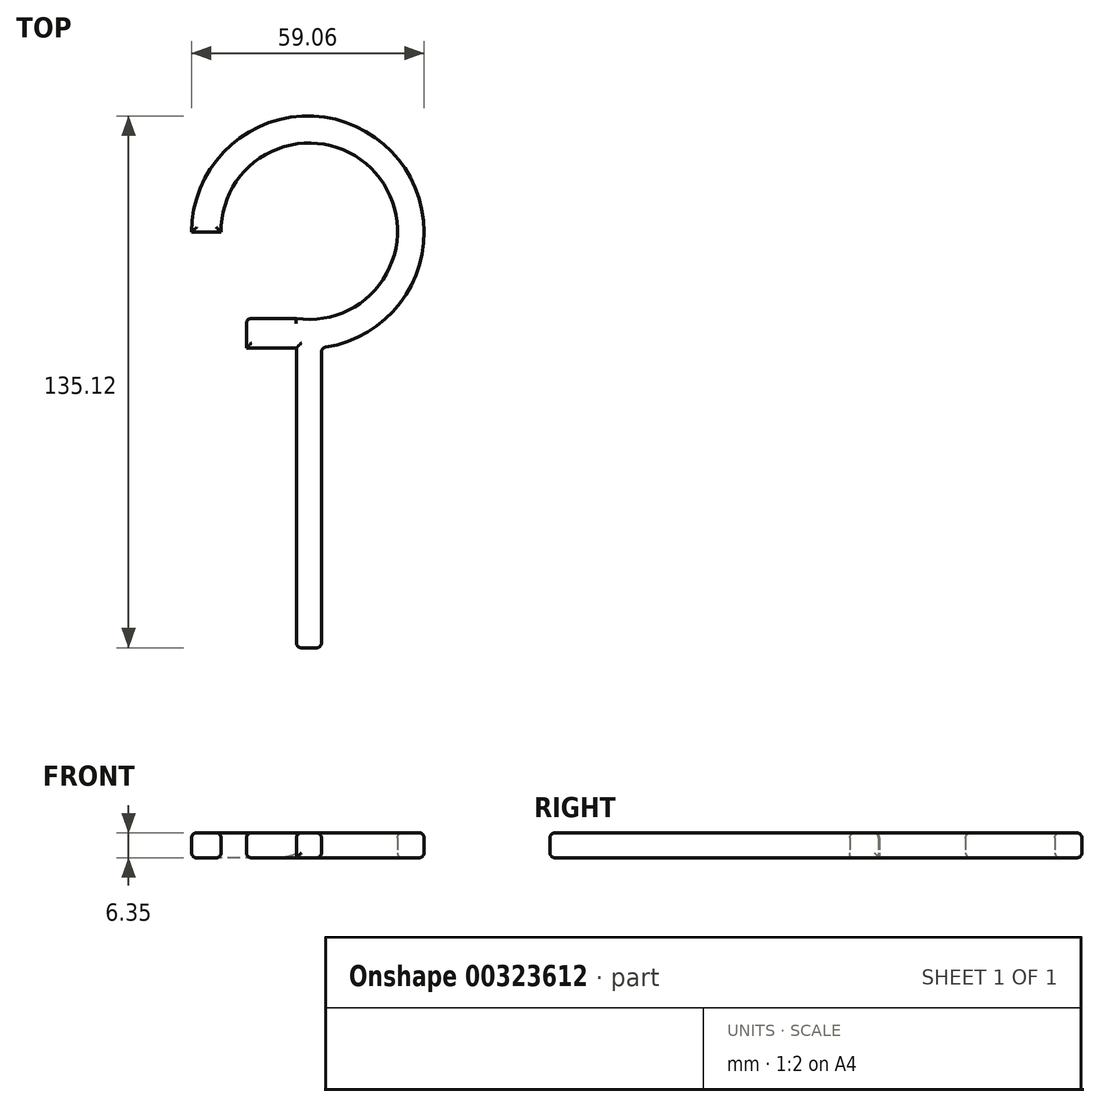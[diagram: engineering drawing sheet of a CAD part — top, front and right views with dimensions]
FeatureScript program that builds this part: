
annotation { "Feature Type Name" : "Feature", "Feature Type Description" : "" }
export const myFeature = defineFeature(function(context is Context, id is Id, definition is map)
    precondition{}
    {
        {
            var Q0;
            Q0=qCreatedBy(makeId("Top.planeOp"),FACE);
            var sketch = newSketch(context, id + "F0", { "sketchPlane" : qUnion([Q0])});
            skArc(sketch, "E0", {"start": v(-2.9, -29.39) * mm, "mid": v(21.88, 19.83) * mm, "end": v(-29.53, 0) * mm});
            skLineSegment(sketch, "E1.left", {"start": v(-2.9, -29.39) * mm, "end": v(-2.9, -105.59) * mm});
            skLineSegment(sketch, "E1.right", {"start": v(3.46, -29.33) * mm, "end": v(3.46, -105.59) * mm});
            skLineSegment(sketch, "E2", {"start": v(-29.53, 0) * mm, "end": v(-22.04, 0) * mm});
            skLineSegment(sketch, "E3", {"start": v(-2.9, -29.39) * mm, "end": v(-2.9, -21.9) * mm});
            skArc(sketch, "E4", {"start": v(-2.9, -21.9) * mm, "mid": v(17.23, 15.02) * mm, "end": v(-22.04, 0) * mm});
            skLineSegment(sketch, "E5", {"start": v(0, -21.9) * mm, "end": v(-15.6, -21.9) * mm});
            skLineSegment(sketch, "E6", {"start": v(-15.6, -21.9) * mm, "end": v(-15.6, -29.39) * mm});
            skLineSegment(sketch, "E7", {"start": v(-15.6, -29.39) * mm, "end": v(-2.9, -29.39) * mm});
            skLineSegment(sketch, "E8", {"start": v(-2.9, -105.59) * mm, "end": v(3.46, -105.59) * mm});
            skSolve(sketch);
        }
        {
            var Q0;
            Q0 = qSketchRegion(id + "F0", true);
            extrude(context, id + "F1", {"entities" : qUnion([Q0]), "depth" : 6.35 * mm});
        }
        {
            var Q0;
            Q0=makeQuery(id+"F1.opExtrude","CAP_EDGE",EDGE,{"disambiguationData":[OSD([sQuery(id+"F0.wireOp",EDGE,"E0")])],"isStart":false});
            var Q1;
            Q1=makeQuery(id+"F1.opExtrude","CAP_FACE",FACE,{"disambiguationData":[OSD([sQuery(id+"F0.wireOp",EDGE,"E0"),sQuery(id+"F0.wireOp",EDGE,"E1.bottom"),sQuery(id+"F0.wireOp",EDGE,"E1.top"),sQuery(id+"F0.wireOp",EDGE,"E1.left"),sQuery(id+"F0.wireOp",EDGE,"E1.right"),sQuery(id+"F0.wireOp",EDGE,"E2"),sQuery(id+"F0.wireOp",EDGE,"E3"),sQuery(id+"F0.wireOp",EDGE,"E4")])],"isStart":false});
            var Q2;
            Q2=makeQuery(id+"F1.opExtrude","CAP_EDGE",EDGE,{"disambiguationData":[OSD([sQuery(id+"F0.wireOp",EDGE,"E6")])],"isStart":true});
            var Q3;
            Q3=makeQuery(id+"F1.opExtrude","SWEPT_EDGE",EDGE,{"disambiguationData":[OSD([sQuery(id+"F0.wireOp",EDGE,"E5"),sQuery(id+"F0.wireOp",EDGE,"E6")])]});
            var Q4;
            Q4=makeQuery(id+"F1.opExtrude","CAP_EDGE",EDGE,{"disambiguationData":[OSD([sQuery(id+"F0.wireOp",EDGE,"E1.top")])],"isStart":true});
            var Q5;
            Q5=makeQuery(id+"F1.opExtrude","SWEPT_EDGE",EDGE,{"disambiguationData":[OSD([sQuery(id+"F0.wireOp",EDGE,"E1.top"),sQuery(id+"F0.wireOp",EDGE,"E1.right")])]});
            fillet(context, id + "F2", {"entities" : qUnion([Q0, Q1, Q2, Q3, Q4, Q5]), "radius" : 1.27 * mm, "tangentPropagation" : true, "allowEdgeOverflow" : false});
        }
        {
            var Q0;
            Q0=makeQuery(id+"F1.opExtrude","CAP_EDGE",EDGE,{"disambiguationData":[OSD([sQuery(id+"F0.wireOp",EDGE,"E0")])],"isStart":true});
            var Q1;
            Q1=makeQuery(id+"F1.opExtrude","CAP_EDGE",EDGE,{"disambiguationData":[OSD([sQuery(id+"F0.wireOp",EDGE,"E4")])],"isStart":true});
            var Q2;
            Q2=makeQuery(id+"F1.opExtrude","CAP_EDGE",EDGE,{"disambiguationData":[OSD([sQuery(id+"F0.wireOp",EDGE,"E2")])],"isStart":true});
            var Q3;
            Q3=makeQuery(id+"F1.opExtrude","SWEPT_EDGE",EDGE,{"disambiguationData":[OSD([sQuery(id+"F0.wireOp",EDGE,"E1.top"),sQuery(id+"F0.wireOp",EDGE,"E1.left")])]});
            fillet(context, id + "F3", {"entities" : qUnion([Q0, Q1, Q2, Q3]), "radius" : 1.27 * mm, "tangentPropagation" : true, "allowEdgeOverflow" : false});
        }
    });
